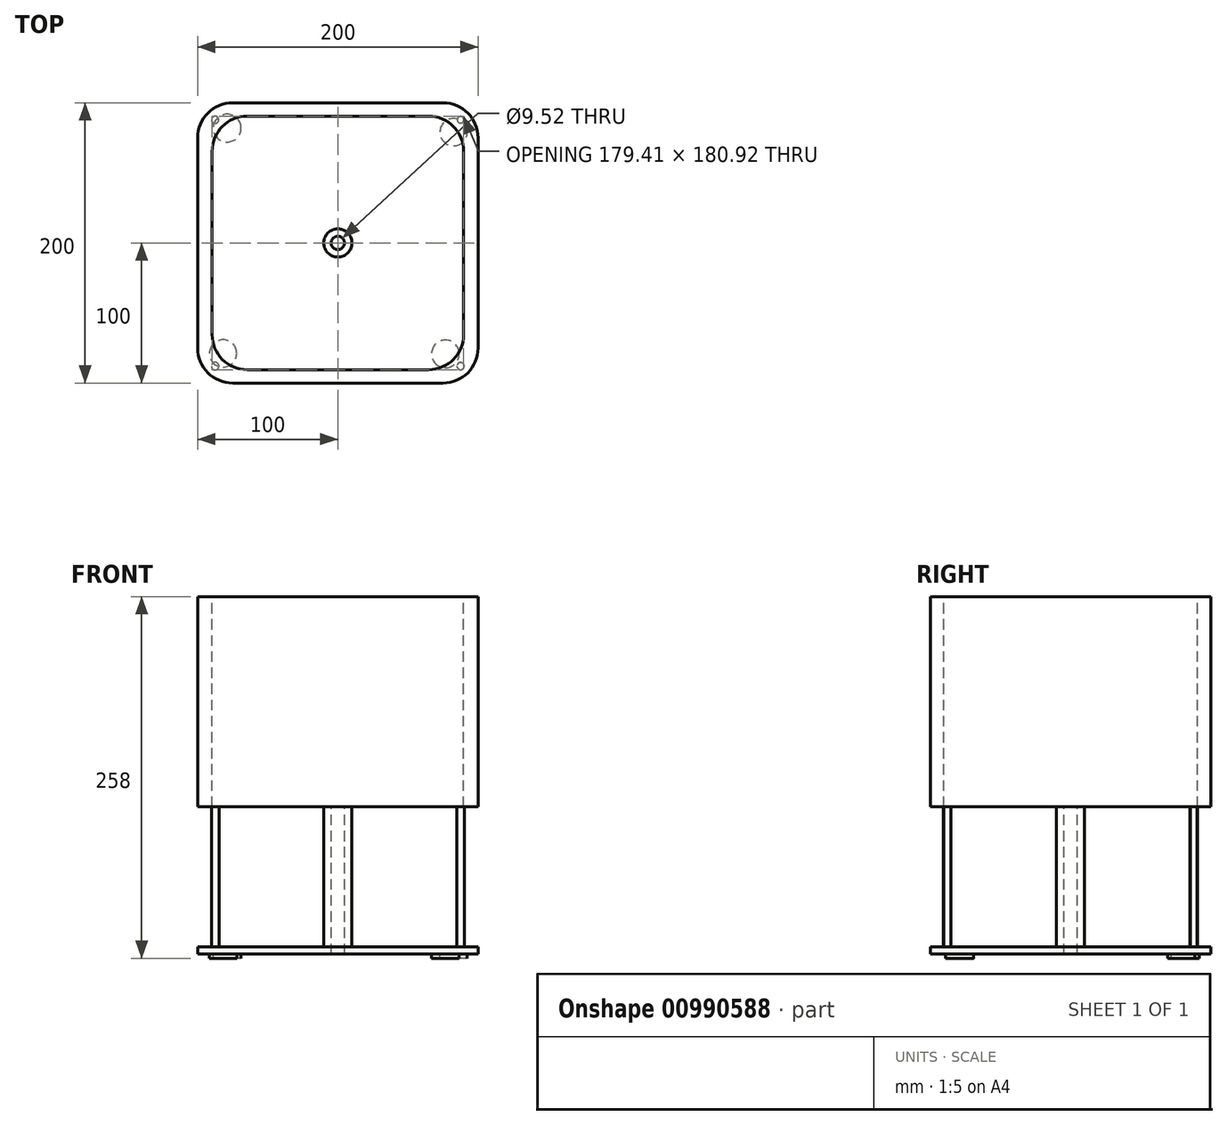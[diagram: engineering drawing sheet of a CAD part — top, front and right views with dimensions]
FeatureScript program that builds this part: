
annotation { "Feature Type Name" : "Feature", "Feature Type Description" : "" }
export const myFeature = defineFeature(function(context is Context, id is Id, definition is map)
    precondition{}
    {
        {
            var Q0;
            Q0=qCreatedBy(makeId("Top.planeOp"),FACE);
            var sketch = newSketch(context, id + "F0", { "sketchPlane" : qUnion([Q0])});
            skLineSegment(sketch, "E0.bottom", {"start": v(75, -100) * mm, "end": v(-75, -100) * mm});
            skLineSegment(sketch, "E0.top", {"start": v(75, 100) * mm, "end": v(-75, 100) * mm});
            skLineSegment(sketch, "E0.left", {"start": v(100, -75) * mm, "end": v(100, 75) * mm});
            skLineSegment(sketch, "E0.right", {"start": v(-100, -75) * mm, "end": v(-100, 75) * mm});
            skPoint(sketch, "E0.middle", {"position": v(0, 0) * mm});
            skPoint(sketch, "E1.visualSharp", {"position": v(-100, 100) * mm});
            skArc(sketch, "E1.filletArc", {"start": v(-75, 100) * mm, "mid": v(-92.68, 92.68) * mm, "end": v(-100, 75) * mm});
            skPoint(sketch, "E2.visualSharp", {"position": v(100, 100) * mm});
            skArc(sketch, "E2.filletArc", {"start": v(100, 75) * mm, "mid": v(92.68, 92.68) * mm, "end": v(75, 100) * mm});
            skPoint(sketch, "E3.visualSharp", {"position": v(100, -100) * mm});
            skArc(sketch, "E3.filletArc", {"start": v(75, -100) * mm, "mid": v(92.68, -92.68) * mm, "end": v(100, -75) * mm});
            skPoint(sketch, "E4.visualSharp", {"position": v(-100, -100) * mm});
            skArc(sketch, "E4.filletArc", {"start": v(-100, -75) * mm, "mid": v(-92.68, -92.68) * mm, "end": v(-75, -100) * mm});
            skSolve(sketch);
        }
        {
            var Q0;
            Q0=makeQuery(id+"F0.imprint","IMPRINT",FACE,{"disambiguationData":[TD([[makeQuery(id+"F0.imprint","IMPRINT",EDGE,{"derivedFrom":sQuery(id+"F0.wireOp",EDGE,"E0.bottom")}),-1.0]])]});
            extrude(context, id + "F1", {"entities" : qUnion([Q0]), "depth" : 5 * mm, "offsetDistance" : 25 * mm});
        }
        {
            var Q0;
            Q0=makeQuery(id+"F1.opExtrude","CAP_FACE",FACE,{"disambiguationData":[OSD([sQuery(id+"F0.wireOp",EDGE,"E0.bottom"),sQuery(id+"F0.wireOp",EDGE,"E0.top"),sQuery(id+"F0.wireOp",EDGE,"E0.left"),sQuery(id+"F0.wireOp",EDGE,"E0.right"),sQuery(id+"F0.wireOp",EDGE,"E1.filletArc"),sQuery(id+"F0.wireOp",EDGE,"E2.filletArc"),sQuery(id+"F0.wireOp",EDGE,"E3.filletArc"),sQuery(id+"F0.wireOp",EDGE,"E4.filletArc")])],"isStart":false});
            var sketch = newSketch(context, id + "F2", { "sketchPlane" : qUnion([Q0])});
            skCircle(sketch, "E5", {"center": v(76.7, -79.16) * mm, "radius": 9.9 * mm});
            skSolve(sketch);
        }
        {
            var Q0;
            Q0 = qSketchRegion(id + "F2", true);
            extrude(context, id + "F3", {"entities" : qUnion([Q0]), "operationType" : NewBodyOperationType.ADD, "oppositeDirection" : true, "depth" : 8 * mm, "offsetDistance" : 25 * mm});
        }
        {
            var Q0;
            Q0=makeQuery(id+"F1.opExtrude","CAP_FACE",FACE,{"disambiguationData":[OSD([sQuery(id+"F0.wireOp",EDGE,"E0.bottom"),sQuery(id+"F0.wireOp",EDGE,"E0.top"),sQuery(id+"F0.wireOp",EDGE,"E0.left"),sQuery(id+"F0.wireOp",EDGE,"E0.right"),sQuery(id+"F0.wireOp",EDGE,"E1.filletArc"),sQuery(id+"F0.wireOp",EDGE,"E2.filletArc"),sQuery(id+"F0.wireOp",EDGE,"E3.filletArc"),sQuery(id+"F0.wireOp",EDGE,"E4.filletArc")])],"isStart":false});
            var sketch = newSketch(context, id + "F4", { "sketchPlane" : qUnion([Q0])});
            skCircle(sketch, "E6", {"center": v(82.53, 79.05) * mm, "radius": 9.76 * mm});
            skSolve(sketch);
        }
        {
            var Q0;
            Q0 = qSketchRegion(id + "F4", true);
            extrude(context, id + "F5", {"entities" : qUnion([Q0]), "operationType" : NewBodyOperationType.ADD, "oppositeDirection" : true, "depth" : 8 * mm, "offsetDistance" : 25 * mm});
        }
        {
            var Q0;
            Q0=makeQuery(id+"F1.opExtrude","CAP_FACE",FACE,{"disambiguationData":[OSD([sQuery(id+"F0.wireOp",EDGE,"E0.bottom"),sQuery(id+"F0.wireOp",EDGE,"E0.top"),sQuery(id+"F0.wireOp",EDGE,"E0.left"),sQuery(id+"F0.wireOp",EDGE,"E0.right"),sQuery(id+"F0.wireOp",EDGE,"E1.filletArc"),sQuery(id+"F0.wireOp",EDGE,"E2.filletArc"),sQuery(id+"F0.wireOp",EDGE,"E3.filletArc"),sQuery(id+"F0.wireOp",EDGE,"E4.filletArc")])],"isStart":false});
            var sketch = newSketch(context, id + "F6", { "sketchPlane" : qUnion([Q0])});
            skCircle(sketch, "E7", {"center": v(-78.94, 81.99) * mm, "radius": 9.97 * mm});
            skSolve(sketch);
        }
        {
            var Q0;
            Q0 = qSketchRegion(id + "F6", true);
            extrude(context, id + "F7", {"entities" : qUnion([Q0]), "operationType" : NewBodyOperationType.ADD, "oppositeDirection" : true, "depth" : 8 * mm, "offsetDistance" : 25 * mm});
        }
        {
            var Q0;
            Q0=makeQuery(id+"F1.opExtrude","CAP_FACE",FACE,{"disambiguationData":[OSD([sQuery(id+"F0.wireOp",EDGE,"E0.bottom"),sQuery(id+"F0.wireOp",EDGE,"E0.top"),sQuery(id+"F0.wireOp",EDGE,"E0.left"),sQuery(id+"F0.wireOp",EDGE,"E0.right"),sQuery(id+"F0.wireOp",EDGE,"E1.filletArc"),sQuery(id+"F0.wireOp",EDGE,"E2.filletArc"),sQuery(id+"F0.wireOp",EDGE,"E3.filletArc"),sQuery(id+"F0.wireOp",EDGE,"E4.filletArc")])],"isStart":false});
            var sketch = newSketch(context, id + "F8", { "sketchPlane" : qUnion([Q0])});
            skCircle(sketch, "E8", {"center": v(-81.85, -78.85) * mm, "radius": 9.76 * mm});
            skSolve(sketch);
        }
        {
            var Q0;
            Q0 = qSketchRegion(id + "F8", true);
            extrude(context, id + "F9", {"entities" : qUnion([Q0]), "operationType" : NewBodyOperationType.ADD, "oppositeDirection" : true, "depth" : 8 * mm, "offsetDistance" : 25 * mm});
        }
        {
            var Q0;
            Q0=makeQuery(id+"F1.opExtrude","CAP_FACE",FACE,{"disambiguationData":[OSD([sQuery(id+"F0.wireOp",EDGE,"E0.bottom"),sQuery(id+"F0.wireOp",EDGE,"E0.top"),sQuery(id+"F0.wireOp",EDGE,"E0.left"),sQuery(id+"F0.wireOp",EDGE,"E0.right"),sQuery(id+"F0.wireOp",EDGE,"E1.filletArc"),sQuery(id+"F0.wireOp",EDGE,"E2.filletArc"),sQuery(id+"F0.wireOp",EDGE,"E3.filletArc"),sQuery(id+"F0.wireOp",EDGE,"E4.filletArc")])],"isStart":false});
            var sketch = newSketch(context, id + "F10", { "sketchPlane" : qUnion([Q0])});
            skCircle(sketch, "E9", {"center": v(0, 0) * mm, "radius": 10.05 * mm});
            skSolve(sketch);
        }
        {
            var Q0;
            Q0 = qSketchRegion(id + "F10", true);
            extrude(context, id + "F11", {"entities" : qUnion([Q0]), "operationType" : NewBodyOperationType.ADD, "depth" : 100 * mm, "offsetDistance" : 25 * mm});
        }
        {
            var Q0;
            Q0=makeQuery(id+"F11.opExtrude","CAP_FACE",FACE,{"disambiguationData":[OSD([sQuery(id+"F10.wireOp",EDGE,"E9")])],"isStart":false});
            var sketch = newSketch(context, id + "F12", { "sketchPlane" : qUnion([Q0])});
            skCircle(sketch, "E10", {"center": v(0, 0) * mm, "radius": 4.76 * mm});
            skSolve(sketch);
        }
        {
            var Q0;
            Q0 = qSketchRegion(id + "F12", true);
            extrude(context, id + "F13", {"entities" : qUnion([Q0]), "operationType" : NewBodyOperationType.REMOVE, "endBound" : BoundingType.THROUGH_ALL, "oppositeDirection" : true, "depth" : 25 * mm, "offsetDistance" : 25 * mm});
        }
        {
            var Q0;
            Q0=makeQuery(id+"F11.opExtrude","CAP_FACE",FACE,{"disambiguationData":[OSD([sQuery(id+"F10.wireOp",EDGE,"E9")])],"isStart":false});
            var sketch = newSketch(context, id + "F14", { "sketchPlane" : qUnion([Q0])});
            skLineSegment(sketch, "E11.bottom", {"start": v(75, -100) * mm, "end": v(-75, -100) * mm});
            skLineSegment(sketch, "E11.top", {"start": v(75, 100) * mm, "end": v(-75, 100) * mm});
            skLineSegment(sketch, "E11.left", {"start": v(100, -75) * mm, "end": v(100, 75) * mm});
            skLineSegment(sketch, "E11.right", {"start": v(-100, -75) * mm, "end": v(-100, 75) * mm});
            skPoint(sketch, "E11.middle", {"position": v(0, 0) * mm});
            skPoint(sketch, "E12.visualSharp", {"position": v(-100, 100) * mm});
            skArc(sketch, "E12.filletArc", {"start": v(-75, 100) * mm, "mid": v(-92.68, 92.68) * mm, "end": v(-100, 75) * mm});
            skPoint(sketch, "E13.visualSharp", {"position": v(-100, -100) * mm});
            skArc(sketch, "E13.filletArc", {"start": v(-100, -75) * mm, "mid": v(-92.68, -92.68) * mm, "end": v(-75, -100) * mm});
            skPoint(sketch, "E14.visualSharp", {"position": v(100, -100) * mm});
            skArc(sketch, "E14.filletArc", {"start": v(75, -100) * mm, "mid": v(92.68, -92.68) * mm, "end": v(100, -75) * mm});
            skPoint(sketch, "E15.visualSharp", {"position": v(100, 100) * mm});
            skArc(sketch, "E15.filletArc", {"start": v(100, 75) * mm, "mid": v(92.68, 92.68) * mm, "end": v(75, 100) * mm});
            skSolve(sketch);
        }
        {
            var Q0;
            Q0 = qSketchRegion(id + "F14", true);
            extrude(context, id + "F15", {"entities" : qUnion([Q0]), "operationType" : NewBodyOperationType.ADD, "depth" : 100 * mm, "offsetDistance" : 25 * mm});
        }
        {
            var Q0;
            Q0=makeQuery(id+"F15.opExtrude","CAP_FACE",FACE,{"disambiguationData":[OSD([sQuery(id+"F14.wireOp",EDGE,"E11.bottom"),sQuery(id+"F14.wireOp",EDGE,"E11.top"),sQuery(id+"F14.wireOp",EDGE,"E11.left"),sQuery(id+"F14.wireOp",EDGE,"E11.right"),sQuery(id+"F14.wireOp",EDGE,"E12.filletArc"),sQuery(id+"F14.wireOp",EDGE,"E13.filletArc"),sQuery(id+"F14.wireOp",EDGE,"E14.filletArc"),sQuery(id+"F14.wireOp",EDGE,"E15.filletArc")])],"isStart":false});
            var sketch = newSketch(context, id + "F16", { "sketchPlane" : qUnion([Q0])});
            skLineSegment(sketch, "E16", {"start": v(100, 0) * mm, "end": v(89.7, 0) * mm});
            skLineSegment(sketch, "E17", {"start": v(0, 100) * mm, "end": v(0, 89.7) * mm});
            skLineSegment(sketch, "E18", {"start": v(-100, 0) * mm, "end": v(-90.08, 0) * mm});
            skLineSegment(sketch, "E19", {"start": v(0, -100) * mm, "end": v(0, -90.46) * mm});
            skLineSegment(sketch, "E20.bottom", {"start": v(64.7, -90.46) * mm, "end": v(-64.7, -90.46) * mm});
            skLineSegment(sketch, "E20.top", {"start": v(64.7, 90.46) * mm, "end": v(-64.7, 90.46) * mm});
            skLineSegment(sketch, "E20.left", {"start": v(89.7, -65.46) * mm, "end": v(89.7, 65.46) * mm});
            skLineSegment(sketch, "E20.right", {"start": v(-89.7, -65.46) * mm, "end": v(-89.7, 65.46) * mm});
            skPoint(sketch, "E20.middle", {"position": v(0, 0) * mm});
            skPoint(sketch, "E21.visualSharp", {"position": v(-89.7, 90.46) * mm});
            skArc(sketch, "E21.filletArc", {"start": v(-64.7, 90.46) * mm, "mid": v(-82.38, 83.14) * mm, "end": v(-89.7, 65.46) * mm});
            skPoint(sketch, "E22.visualSharp", {"position": v(-89.7, -90.46) * mm});
            skArc(sketch, "E22.filletArc", {"start": v(-89.7, -65.46) * mm, "mid": v(-82.38, -83.14) * mm, "end": v(-64.7, -90.46) * mm});
            skPoint(sketch, "E23.visualSharp", {"position": v(89.7, -90.46) * mm});
            skArc(sketch, "E23.filletArc", {"start": v(64.7, -90.46) * mm, "mid": v(82.38, -83.14) * mm, "end": v(89.7, -65.46) * mm});
            skPoint(sketch, "E24.visualSharp", {"position": v(89.7, 90.46) * mm});
            skArc(sketch, "E24.filletArc", {"start": v(89.7, 65.46) * mm, "mid": v(82.38, 83.14) * mm, "end": v(64.7, 90.46) * mm});
            skSolve(sketch);
        }
        {
            var Q0;
            Q0=makeQuery(id+"F16.imprint","IMPRINT",FACE,{"disambiguationData":[TD([[makeQuery(id+"F16.imprint","IMPRINT",EDGE,{"derivedFrom":sQuery(id+"F16.wireOp",EDGE,"E20.right")}),-1.0]])]});
            extrude(context, id + "F17", {"entities" : qUnion([Q0]), "operationType" : NewBodyOperationType.REMOVE, "oppositeDirection" : true, "depth" : 100 * mm, "offsetDistance" : 25 * mm});
        }
        {
            var Q0;
            Q0=makeQuery(id+"F15.opExtrude","CAP_FACE",FACE,{"disambiguationData":[OSD([sQuery(id+"F14.wireOp",EDGE,"E11.bottom"),sQuery(id+"F14.wireOp",EDGE,"E11.top"),sQuery(id+"F14.wireOp",EDGE,"E11.left"),sQuery(id+"F14.wireOp",EDGE,"E11.right"),sQuery(id+"F14.wireOp",EDGE,"E12.filletArc"),sQuery(id+"F14.wireOp",EDGE,"E13.filletArc"),sQuery(id+"F14.wireOp",EDGE,"E14.filletArc"),sQuery(id+"F14.wireOp",EDGE,"E15.filletArc")])],"isStart":false});
            extrude(context, id + "F18", {"entities" : qUnion([Q0]), "operationType" : NewBodyOperationType.ADD, "depth" : 50 * mm, "offsetDistance" : 25 * mm});
        }
        {
            var Q0;
            {var subQ0=sQuery(id+"F14.wireOp",EDGE,"E11.left");var subQ1=sQuery(id+"F14.wireOp",EDGE,"E11.top");var subQ2=sQuery(id+"F14.wireOp",EDGE,"E11.bottom");var subQ3=sQuery(id+"F14.wireOp",EDGE,"E11.right");var subQ4=sQuery(id+"F14.wireOp",EDGE,"E12.filletArc");var subQ5=sQuery(id+"F14.wireOp",EDGE,"E13.filletArc");var subQ6=sQuery(id+"F14.wireOp",EDGE,"E14.filletArc");var subQ7=sQuery(id+"F14.wireOp",EDGE,"E15.filletArc");Q0=makeQuery(id+"F15.boolean.opBoolean","SPLIT",FACE,{"disambiguationData":[TD([makeQuery(id+"F11.opExtrude","SWEPT_FACE",FACE,{"disambiguationData":[OSD([sQuery(id+"F10.wireOp",EDGE,"E9")])]})])],"derivedFrom":makeQuery(id+"F15.opExtrude","CAP_FACE",FACE,{"disambiguationData":[OSD([subQ2,subQ1,subQ0,subQ3,subQ4,subQ5,subQ6,subQ7])],"isStart":true})});}
            var sketch = newSketch(context, id + "F19", { "sketchPlane" : qUnion([Q0])});
            skCircle(sketch, "E25", {"center": v(-87.53, 87.9) * mm, "radius": 2.7 * mm});
            skSolve(sketch);
        }
        {
            var Q0;
            Q0 = qSketchRegion(id + "F19", true);
            extrude(context, id + "F20", {"entities" : qUnion([Q0]), "endBound" : BoundingType.UP_TO_NEXT, "depth" : 25 * mm, "offsetDistance" : 25 * mm});
        }
        {
            var Q0;
            {var subQ0=sQuery(id+"F14.wireOp",EDGE,"E11.left");var subQ1=sQuery(id+"F14.wireOp",EDGE,"E11.top");var subQ2=sQuery(id+"F14.wireOp",EDGE,"E11.bottom");var subQ3=sQuery(id+"F14.wireOp",EDGE,"E11.right");var subQ4=sQuery(id+"F14.wireOp",EDGE,"E12.filletArc");var subQ5=sQuery(id+"F14.wireOp",EDGE,"E13.filletArc");var subQ6=sQuery(id+"F14.wireOp",EDGE,"E14.filletArc");var subQ7=sQuery(id+"F14.wireOp",EDGE,"E15.filletArc");Q0=makeQuery(id+"F15.boolean.opBoolean","SPLIT",FACE,{"disambiguationData":[TD([makeQuery(id+"F11.opExtrude","SWEPT_FACE",FACE,{"disambiguationData":[OSD([sQuery(id+"F10.wireOp",EDGE,"E9")])]})])],"derivedFrom":makeQuery(id+"F15.opExtrude","CAP_FACE",FACE,{"disambiguationData":[OSD([subQ2,subQ1,subQ0,subQ3,subQ4,subQ5,subQ6,subQ7])],"isStart":true})});}
            var sketch = newSketch(context, id + "F21", { "sketchPlane" : qUnion([Q0])});
            skCircle(sketch, "E26", {"center": v(-87.53, -87.9) * mm, "radius": 2.62 * mm});
            skSolve(sketch);
        }
        {
            var Q0;
            Q0 = qSketchRegion(id + "F21", true);
            extrude(context, id + "F22", {"entities" : qUnion([Q0]), "endBound" : BoundingType.UP_TO_NEXT, "depth" : 25 * mm, "offsetDistance" : 25 * mm});
        }
        {
            var Q0;
            {var subQ0=sQuery(id+"F14.wireOp",EDGE,"E11.left");var subQ1=sQuery(id+"F14.wireOp",EDGE,"E11.top");var subQ2=sQuery(id+"F14.wireOp",EDGE,"E11.bottom");var subQ3=sQuery(id+"F14.wireOp",EDGE,"E11.right");var subQ4=sQuery(id+"F14.wireOp",EDGE,"E12.filletArc");var subQ5=sQuery(id+"F14.wireOp",EDGE,"E13.filletArc");var subQ6=sQuery(id+"F14.wireOp",EDGE,"E14.filletArc");var subQ7=sQuery(id+"F14.wireOp",EDGE,"E15.filletArc");Q0=makeQuery(id+"F15.boolean.opBoolean","SPLIT",FACE,{"disambiguationData":[TD([makeQuery(id+"F11.opExtrude","SWEPT_FACE",FACE,{"disambiguationData":[OSD([sQuery(id+"F10.wireOp",EDGE,"E9")])]})])],"derivedFrom":makeQuery(id+"F15.opExtrude","CAP_FACE",FACE,{"disambiguationData":[OSD([subQ2,subQ1,subQ0,subQ3,subQ4,subQ5,subQ6,subQ7])],"isStart":true})});}
            var sketch = newSketch(context, id + "F23", { "sketchPlane" : qUnion([Q0])});
            skCircle(sketch, "E27", {"center": v(87.53, -87.9) * mm, "radius": 2.36 * mm});
            skSolve(sketch);
        }
        {
            var Q0;
            Q0 = qSketchRegion(id + "F23", true);
            extrude(context, id + "F24", {"entities" : qUnion([Q0]), "endBound" : BoundingType.UP_TO_NEXT, "depth" : 25 * mm, "offsetDistance" : 25 * mm});
        }
        {
            var Q0;
            {var subQ0=sQuery(id+"F14.wireOp",EDGE,"E11.left");var subQ1=sQuery(id+"F14.wireOp",EDGE,"E11.top");var subQ2=sQuery(id+"F14.wireOp",EDGE,"E11.bottom");var subQ3=sQuery(id+"F14.wireOp",EDGE,"E11.right");var subQ4=sQuery(id+"F14.wireOp",EDGE,"E12.filletArc");var subQ5=sQuery(id+"F14.wireOp",EDGE,"E13.filletArc");var subQ6=sQuery(id+"F14.wireOp",EDGE,"E14.filletArc");var subQ7=sQuery(id+"F14.wireOp",EDGE,"E15.filletArc");Q0=makeQuery(id+"F15.boolean.opBoolean","SPLIT",FACE,{"disambiguationData":[TD([makeQuery(id+"F11.opExtrude","SWEPT_FACE",FACE,{"disambiguationData":[OSD([sQuery(id+"F10.wireOp",EDGE,"E9")])]})])],"derivedFrom":makeQuery(id+"F15.opExtrude","CAP_FACE",FACE,{"disambiguationData":[OSD([subQ2,subQ1,subQ0,subQ3,subQ4,subQ5,subQ6,subQ7])],"isStart":true})});}
            var sketch = newSketch(context, id + "F25", { "sketchPlane" : qUnion([Q0])});
            skCircle(sketch, "E28", {"center": v(87.53, 87.9) * mm, "radius": 2.6 * mm});
            skSolve(sketch);
        }
        {
            var Q0;
            Q0 = qSketchRegion(id + "F25", true);
            extrude(context, id + "F26", {"entities" : qUnion([Q0]), "endBound" : BoundingType.UP_TO_NEXT, "depth" : 25 * mm, "offsetDistance" : 25 * mm});
        }
    });
